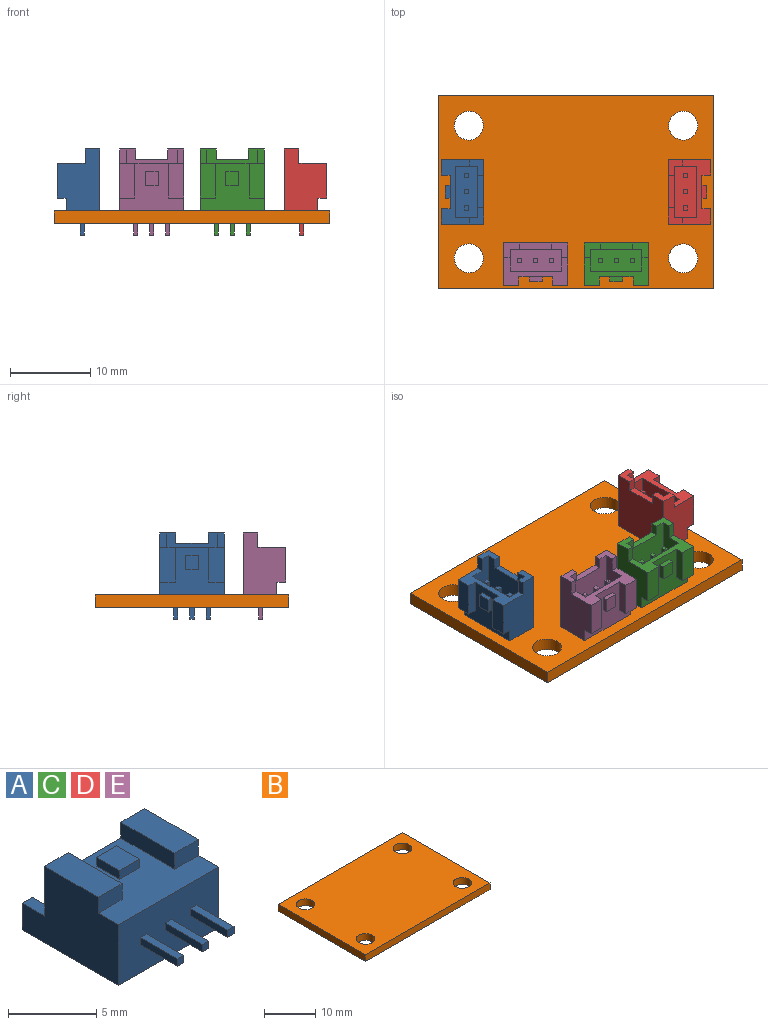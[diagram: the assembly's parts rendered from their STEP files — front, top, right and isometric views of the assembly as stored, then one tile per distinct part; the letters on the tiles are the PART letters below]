
ASSEMBLY  parts=5 mates=4
PART A: 59 faces, bbox 8x10.7x5.3 mm
  f0: plane 3x0.5mm, normal (1,0,0), area 1.5mm2, adj f1,f2,f3,f4
  f1: plane 0.5x0.5mm, normal (0,-1,0), area 0.2mm2, adj f0,f2,f3,f5
  f2: plane 3x0.5mm, normal (0,0,1), area 1.5mm2, adj f0,f1,f4,f5
  f3: plane 3x0.5mm, normal (0,0,-1), area 1.5mm2, adj f0,f1,f4,f5
  f4: plane 8x4.2mm, normal (0,-1,0), area 32.8mm2, adj f0,f2,f3,f5,f6,f7,f8,f9
  f5: plane 3x0.5mm, normal (-1,0,0), area 1.5mm2, adj f1,f2,f3,f4
  f6: plane 7.7x5.3mm, normal (1,0,0), area 32.8mm2, adj f4,f8,f14,f18,f19,f20,f21,f22
  f7: plane 3x0.5mm, normal (-1,0,0), area 1.5mm2, adj f4,f10,f13,f23
  f8: plane 8x5.9mm, normal (0,0,1), area 27.9mm2, adj f4,f6,f12,f20,f22,f24,f25,f26
  f9: plane 3x0.5mm, normal (-1,0,0), area 1.5mm2, adj f4,f11,f15,f31
  f10: plane 3x0.5mm, normal (0,0,-1), area 1.5mm2, adj f4,f7,f16,f23
  f11: plane 3x0.5mm, normal (0,0,-1), area 1.5mm2, adj f4,f9,f17,f31
  f12: plane 7.7x5.3mm, normal (-1,0,0), area 32.8mm2, adj f4,f8,f14,f20,f26,f32,f33,f34
  f13: plane 3x0.5mm, normal (0,0,1), area 1.5mm2, adj f4,f7,f16,f23
  f14: plane 8x7.7mm, normal (0,0,-1), area 56.4mm2, adj f4,f6,f12,f18,f32,f35,f36,f37
  f15: plane 3x0.5mm, normal (0,0,1), area 1.5mm2, adj f4,f9,f17,f31
  f16: plane 3x0.5mm, normal (1,0,0), area 1.5mm2, adj f4,f10,f13,f23
  f17: plane 3x0.5mm, normal (1,0,0), area 1.5mm2, adj f4,f11,f15,f31
  f18: plane 2x1.85mm, normal (0,1,0), area 2.4mm2, adj f6,f14,f21,f37,f38,f39
  f19: plane 4.3x1.9mm, normal (0,0,1), area 8.2mm2, adj f6,f20,f22,f28
  f20: plane 8x3.45mm, normal (0,1,0), area 12.4mm2, adj f6,f8,f12,f19,f21,f25,f28,f33
  f21: plane 1.8x0.8mm, normal (0,0,1), area 1.4mm2, adj f6,f18,f20,f39
  f22: plane 1.9x1.1mm, normal (0,-1,0), area 2.1mm2, adj f6,f8,f19,f28
  f23: plane 0.5x0.5mm, normal (0,-1,0), area 0.2mm2, adj f7,f10,f13,f16
  f24: plane 1.84x0.6mm, normal (1,0,0), area 1.1mm2, adj f8,f27,f30,f42
  f25: plane 4.3x1.1mm, normal (1,0,0), area 4.7mm2, adj f8,f20,f26,f33
  f26: plane 1.9x1.1mm, normal (0,-1,0), area 2.1mm2, adj f8,f12,f25,f33
  f27: plane 1.6x0.6mm, normal (0,1,0), area 1mm2, adj f8,f24,f29,f42
  f28: plane 4.3x1.1mm, normal (-1,0,0), area 4.7mm2, adj f8,f19,f20,f22
  f29: plane 1.84x0.6mm, normal (-1,0,0), area 1.1mm2, adj f8,f27,f30,f42
  f30: plane 1.6x0.6mm, normal (0,-1,0), area 1mm2, adj f8,f24,f29,f42
  f31: plane 0.5x0.5mm, normal (0,-1,0), area 0.2mm2, adj f9,f11,f15,f17
  f32: plane 2x1.85mm, normal (0,1,0), area 2.4mm2, adj f12,f14,f34,f36,f38,f40
  f33: plane 4.3x1.9mm, normal (0,0,1), area 8.2mm2, adj f12,f20,f25,f26
  f34: plane 1.8x0.8mm, normal (0,0,1), area 1.4mm2, adj f12,f20,f32,f40
  f35: plane 4x0.8mm, normal (0,1,0), area 3.2mm2, adj f14,f36,f37,f38
  f36: plane 1.3x0.8mm, normal (1,0,0), area 1mm2, adj f14,f32,f35,f38
  f37: plane 1.3x0.8mm, normal (-1,0,0), area 1mm2, adj f14,f18,f35,f38
  f38: plane 6.4x5.8mm, normal (0,0,1), area 31.9mm2, adj f18,f32,f35,f36,f37,f39,f40,f43
  f39: plane 5.8x2.7mm, normal (-1,0,0), area 12.7mm2, adj f18,f20,f21,f38,f41,f43
  f40: plane 5.8x2.7mm, normal (1,0,0), area 12.7mm2, adj f20,f32,f34,f38,f41,f43
  f41: plane 6.4x4mm, normal (0,0,-1), area 25.6mm2, adj f20,f39,f40,f43
  f42: plane 1.84x1.6mm, normal (0,0,1), area 2.9mm2, adj f24,f27,f29,f30
  f43: plane 6.4x2.7mm, normal (0,1,0), area 16.5mm2, adj f38,f39,f40,f41,f44,f45,f46,f47
  f44: plane 3.2x0.5mm, normal (-1,0,0), area 1.6mm2, adj f43,f47,f55,f56
  f45: plane 3.2x0.5mm, normal (-1,0,0), area 1.6mm2, adj f43,f48,f51,f57
  f46: plane 3.2x0.5mm, normal (1,0,0), area 1.6mm2, adj f43,f48,f51,f57
  f47: plane 3.2x0.5mm, normal (0,0,1), area 1.6mm2, adj f43,f44,f50,f56
  f48: plane 3.2x0.5mm, normal (0,0,1), area 1.6mm2, adj f43,f45,f46,f57
  f49: plane 3.2x0.5mm, normal (-1,0,0), area 1.6mm2, adj f43,f52,f54,f58
  f50: plane 3.2x0.5mm, normal (1,0,0), area 1.6mm2, adj f43,f47,f55,f56
  f51: plane 3.2x0.5mm, normal (0,0,-1), area 1.6mm2, adj f43,f45,f46,f57
  f52: plane 3.2x0.5mm, normal (0,0,1), area 1.6mm2, adj f43,f49,f53,f58
  f53: plane 3.2x0.5mm, normal (1,0,0), area 1.6mm2, adj f43,f52,f54,f58
  f54: plane 3.2x0.5mm, normal (0,0,-1), area 1.6mm2, adj f43,f49,f53,f58
  f55: plane 3.2x0.5mm, normal (0,0,-1), area 1.6mm2, adj f43,f44,f50,f56
  f56: plane 0.5x0.5mm, normal (0,1,0), area 0.2mm2, adj f44,f47,f50,f55
  f57: plane 0.5x0.5mm, normal (0,1,0), area 0.2mm2, adj f45,f46,f48,f51
  f58: plane 0.5x0.5mm, normal (0,1,0), area 0.2mm2, adj f49,f52,f53,f54
PART B: 10 faces, bbox 34.3x24.1x1.6 mm
  f0: plane 24.1x1.6mm, normal (-1,0,0), area 38.6mm2, adj f1,f6,f8,f9
  f1: plane 34.3x1.6mm, normal (0,-1,0), area 54.9mm2, adj f0,f2,f8,f9
  f2: plane 24.1x1.6mm, normal (1,0,0), area 38.6mm2, adj f1,f6,f8,f9
  f3: cylinder r=1.8mm len=3.6mm, axis (0,0,-1), area 18.1mm2, adj f8,f9
  f4: cylinder r=1.8mm len=3.6mm, axis (0,0,-1), area 18.1mm2, adj f8,f9
  f5: cylinder r=1.8mm len=3.6mm, axis (0,0,-1), area 18.1mm2, adj f8,f9
  f6: plane 34.3x1.6mm, normal (0,1,0), area 54.9mm2, adj f0,f2,f8,f9
  f7: cylinder r=1.8mm len=3.6mm, axis (0,0,-1), area 18.1mm2, adj f8,f9
  f8: plane 34.3x24.1mm, normal (0,0,1), area 785.9mm2, adj f0,f1,f2,f3,f4,f5,f6,f7
  f9: plane 34.3x24.1mm, normal (0,0,-1), area 785.9mm2, adj f0,f1,f2,f3,f4,f5,f6,f7
PART C: same geometry as A
PART D: same geometry as A
PART E: same geometry as A
PLACE A rot(axis=(0.58,-0.58,-0.58),120deg) t=(3.5,12.05,5.45)mm
PLACE B at identity fixed
PLACE C rot(axis=(1,0,0),90deg) t=(22.15,3.5,5.45)mm
PLACE D rot(axis=(0.58,0.58,0.58),120deg) t=(30.8,12.05,5.45)mm
PLACE E rot(axis=(1,0,0),90deg) t=(12.15,3.5,5.45)mm
MATE fastened C.f4 <-> B.f8  axis (0,0,-1) through (22.15,1.5,1.6)mm
MATE fastened A.f4 <-> B.f8  axis (0,0,-1) through (1.5,12.05,1.6)mm
MATE fastened D.f4 <-> B.f8  axis (0,0,-1) through (32.8,12.05,1.6)mm
MATE fastened E.f4 <-> B.f8  axis (0,0,-1) through (12.15,1.5,1.6)mm
